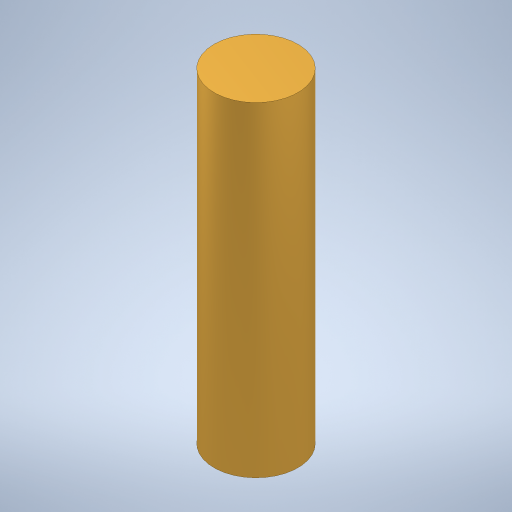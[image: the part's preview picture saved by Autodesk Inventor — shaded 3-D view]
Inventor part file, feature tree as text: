
AUTODESK INVENTOR PART (.ipt)
format: ipt  version: 2023 (Build 270158000, 158)  size: 231,424 bytes
history: native  units: mm
features: other x1, extrude x1, sketch x1
ambient origin geometry x8: Origin, YZ Plane, XZ Plane, XY Plane, X Axis, Y Axis, Z Axis, Center Point
bodies: Body1 (feature_tree)
feature tree (3):
  other  "Sólido1"
  extrude  "Extrusão1"  Depth=31.0mm TaperAngle=0.0deg
  sketch  "Esboço1"  dims[d1=8.0mm d2=31.0mm d3=0.0mm]
